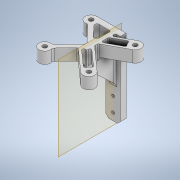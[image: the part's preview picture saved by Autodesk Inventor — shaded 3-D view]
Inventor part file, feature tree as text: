
AUTODESK INVENTOR PART (.ipt)
format: ipt  version: 2020 (Build 240168000, 168)  size: 593,408 bytes
history: native  units: mm
features: projected_geometry x19, extrude x12, sketch x12, fillet x11, other x3, plane x1, chamfer x1, thicken_offset x1, reference x1
ambient origin geometry x8: Origin, YZ Plane, XZ Plane, XY Plane, X Axis, Y Axis, Z Axis, Center Point
bodies: Solid1 (feature_tree)
feature tree (61):
  extrude  "Extrusion1"  Depth=10.0mm
  extrude  "Extrusion2"  Depth=2.0mm
  plane  "Work Plane1"
  extrude  "Extrusion3"  Depth=10.0mm
  extrude  "Extrusion4"  Depth=20.0mm
  extrude  "Extrusion5"  Depth=40.0mm
  extrude  "Extrusion6"  Depth=30.0mm
  extrude  "Extrusion7"  Depth=3.0mm TaperAngle=0.0deg
  extrude  "Extrusion8"  Depth=32.0mm
  chamfer  "Chamfer1"  Distance=3.0mm
  extrude  "Extrusion9"  Depth=2.0mm
  fillet  "Fillet1"  Radius=8.0mm
  fillet  "Fillet3"  Radius=8.0mm
  fillet  "Fillet4"  Radius=8.0mm
  fillet  "Fillet5"  Radius=5.0mm
  thicken_offset  "Thicken1"
  extrude  "Extrusion11"  Depth=2.0mm
  extrude  "Extrusion12"  Depth=2.0mm
  fillet  "Fillet7"  Radius=5.0mm
  fillet  "Fillet8"  Radius=5.0mm
  fillet  "Fillet9"  Radius=20.0mm
  fillet  "Fillet10"  Radius=2.0mm
  extrude  "Extrusion13"  Depth=2.0mm TaperAngle=0.0deg
  fillet  "Fillet11"  Radius=1.5mm
  fillet  "Fillet12"  Radius=3.0mm
  fillet  "Fillet13"  Radius=1.0mm
  sketch  "Sketch1"  dims[d0=10.0mm d1=20.0mm]
  reference  "Reference1"
  sketch  "Sketch2"  dims[d2=2.0mm d3=2.0mm]
  projected_geometry  "Projected Loop1"
  sketch  "Sketch3"  dims[d4=10.0mm d5=30.0mm]
  projected_geometry  "Projected Loop2"
  projected_geometry  "Projected Loop3"
  sketch  "Sketch4"  dims[d6=3.0mm d7=0.0mm d8=20.0mm]
  projected_geometry  "Projected Loop4"
  sketch  "Sketch5"  dims[d9=40.0mm d10=40.0mm]
  projected_geometry  "Projected Loop5"
  sketch  "Sketch6"  dims[d11=3.0mm d12=0.0mm d13=30.0mm]
  projected_geometry  "Projected Loop6"
  sketch  "Sketch7"  dims[d14=28.0mm d15=3.0mm d16=0.0mm]
  projected_geometry  "Projected Loop7"
  projected_geometry  "Projected Loop8"
  projected_geometry  "Projected Loop9"
  projected_geometry  "Projected Loop10"
  projected_geometry  "Projected Loop11"
  sketch  "Sketch8"  dims[d17=30.5mm d18=32.0mm]
  projected_geometry  "Projected Loop12"
  sketch  "Sketch9"  dims[d19=3.0mm]
  projected_geometry  "Projected Loop13"
  sketch  "Sketch11"  dims[d20=3.0mm]
  projected_geometry  "Projected Loop15"
  sketch  "Sketch12"  dims[d21=3.0mm]
  projected_geometry  "Projected Loop16"
  projected_geometry  "Projected Loop17"
  projected_geometry  "Projected Loop18"
  sketch  "Sketch13"  dims[d22=3.0mm d23=3.0mm d24=0.0mm d25=8.0mm d26=8.0mm d27=8.0mm d28=8.0mm d29=5.0mm d30=0.0mm d31=3.0mm d32=3.0mm d33=5.0mm d34=0.0mm d35=5.0mm d36=0.0mm d37=20.0mm d38=0.0mm d39=2.0mm d40=2.0mm d41=45.0deg d42=20.0mm d43=0.0mm d44=1.5mm d46=3.0mm d47=1.0mm d48=3.0mm d55=1.0mm d56=1.0mm d57=8.0mm d58=8.0mm d59=20.0mm d60=0.0mm d61=8.0mm d62=1.5mm d63=1.5mm d64=20.0mm d65=0.0mm d66=1.0mm d67=2.0mm d68=1.0mm d69=1.0mm d70=8.0mm d71=1.5mm d72=1.5mm d73=20.0mm d74=0.0mm d75=1.0mm d76=2.0mm d77=2.0mm]
  projected_geometry  "Projected Loop19"
  projected_geometry  "Projected Loop20"
  parser-record x1  (decoder bookkeeping rows leaked as tree rows — omitted from the tree; the rows remain in map.json)
  other  "leg_1.iam"
  other  "leg_holder_2:1"
note: 1 file-system path scrubbed to <path> (originals preserved in map.json)
